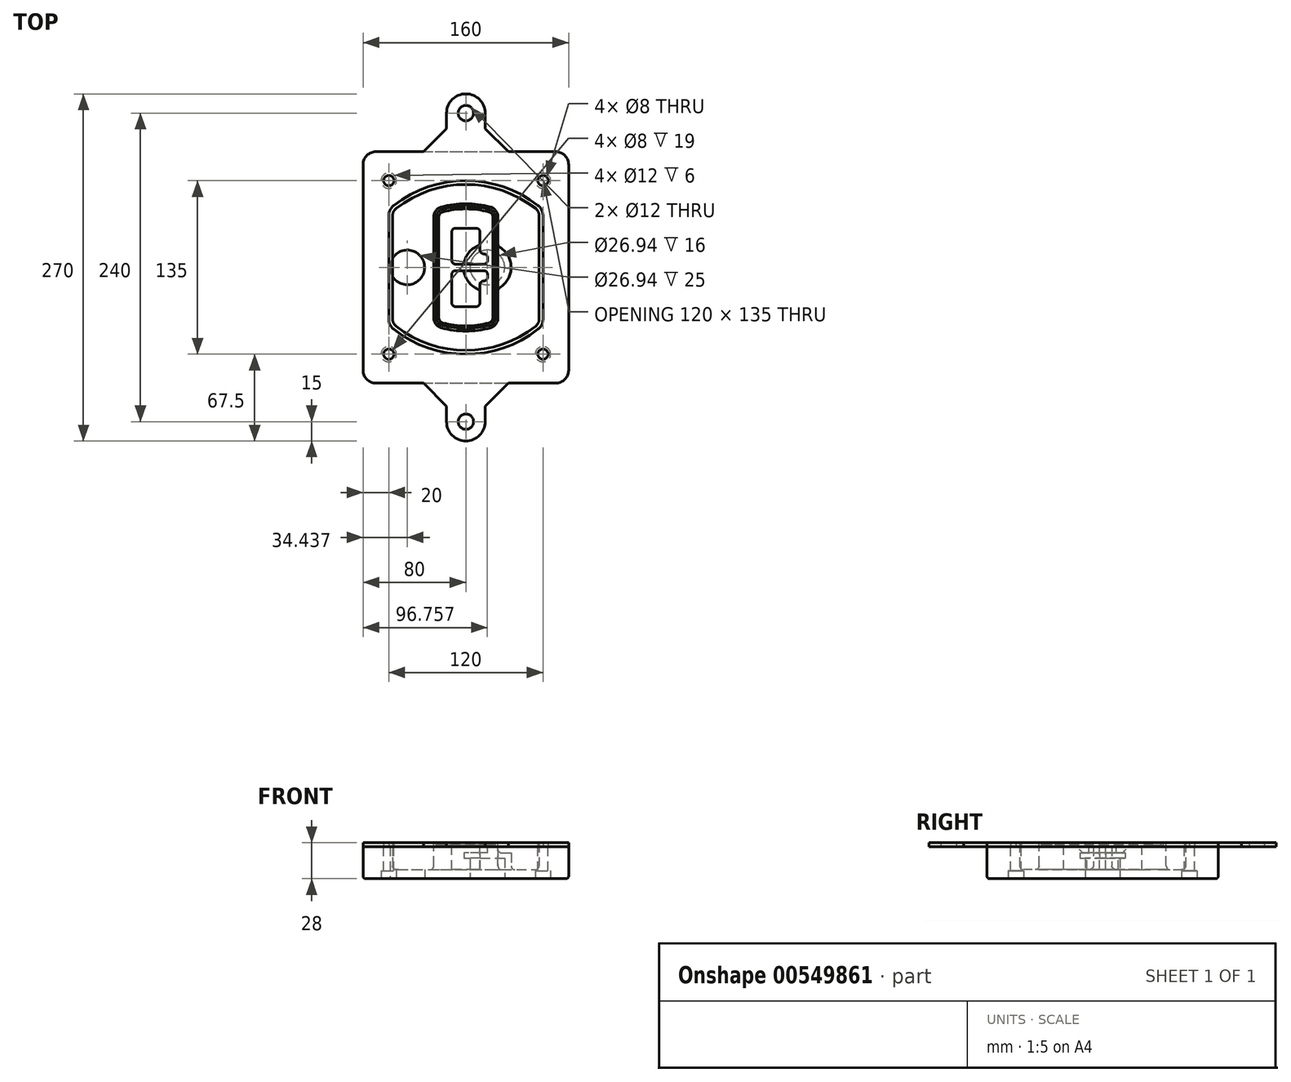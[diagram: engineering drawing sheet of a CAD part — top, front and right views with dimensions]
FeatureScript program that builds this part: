
annotation { "Feature Type Name" : "Feature", "Feature Type Description" : "" }
export const myFeature = defineFeature(function(context is Context, id is Id, definition is map)
    precondition{}
    {
        {
            var Q0;
            Q0=qCreatedBy(makeId("Top.planeOp"),FACE);
            var sketch = newSketch(context, id + "F0", { "sketchPlane" : qUnion([Q0])});
            skPoint(sketch, "E0.rect.middle", {"position": v(0, 0) * mm});
            skLineSegment(sketch, "E1.bottom", {"start": v(-70, -90) * mm, "end": v(70, -90) * mm});
            skLineSegment(sketch, "E1.top", {"start": v(-70, 90) * mm, "end": v(70, 90) * mm});
            skLineSegment(sketch, "E1.left", {"start": v(-80, -80) * mm, "end": v(-80, 80) * mm});
            skLineSegment(sketch, "E1.right", {"start": v(80, -80) * mm, "end": v(80, 80) * mm});
            skLineSegment(sketch, "E2", {"start": v(-80, 90) * mm, "end": v(80, -90) * mm, "construction": true});
            skLineSegment(sketch, "E3", {"start": v(80, 90) * mm, "end": v(-80, -90) * mm, "construction": true});
            skCircle(sketch, "E4", {"center": v(-60, 67.5) * mm, "radius": 4 * mm});
            skCircle(sketch, "E5", {"center": v(60, 67.5) * mm, "radius": 4 * mm});
            skCircle(sketch, "E6", {"center": v(60, -67.5) * mm, "radius": 4 * mm});
            skCircle(sketch, "E7", {"center": v(-60, -67.5) * mm, "radius": 4 * mm});
            skLineSegment(sketch, "E8", {"start": v(-60, 67.5) * mm, "end": v(60, 67.5) * mm, "construction": true});
            skLineSegment(sketch, "E9", {"start": v(60, 67.5) * mm, "end": v(60, -67.5) * mm, "construction": true});
            skLineSegment(sketch, "E10", {"start": v(60, -67.5) * mm, "end": v(-60, -67.5) * mm, "construction": true});
            skLineSegment(sketch, "E11", {"start": v(-60, -67.5) * mm, "end": v(-60, 67.5) * mm, "construction": true});
            skLineSegment(sketch, "E12", {"start": v(-60, 40.3) * mm, "end": v(-60, -40.3) * mm});
            skLineSegment(sketch, "E13", {"start": v(60, 40.3) * mm, "end": v(60, -40.3) * mm});
            skArc(sketch, "E14", {"start": v(56.15, 48.18) * mm, "mid": v(0, 67.5) * mm, "end": v(-56.15, 48.18) * mm});
            skArc(sketch, "E15", {"start": v(-56.15, -48.18) * mm, "mid": v(0, -67.5) * mm, "end": v(56.15, -48.18) * mm});
            skLineSegment(sketch, "E16", {"start": v(-60, 0) * mm, "end": v(60, 0) * mm, "construction": true});
            skPoint(sketch, "E17.visualSharp", {"position": v(-60, -45) * mm});
            skArc(sketch, "E17.filletArc", {"start": v(-60, -40.3) * mm, "mid": v(-58.99, -44.68) * mm, "end": v(-56.15, -48.18) * mm});
            skPoint(sketch, "E18.visualSharp", {"position": v(-60, 45) * mm});
            skArc(sketch, "E18.filletArc", {"start": v(-56.15, 48.18) * mm, "mid": v(-58.99, 44.68) * mm, "end": v(-60, 40.3) * mm});
            skPoint(sketch, "E19.visualSharp", {"position": v(60, 45) * mm});
            skArc(sketch, "E19.filletArc", {"start": v(60, 40.3) * mm, "mid": v(58.99, 44.68) * mm, "end": v(56.15, 48.18) * mm});
            skPoint(sketch, "E20.visualSharp", {"position": v(60, -45) * mm});
            skArc(sketch, "E20.filletArc", {"start": v(56.15, -48.18) * mm, "mid": v(58.99, -44.68) * mm, "end": v(60, -40.3) * mm});
            skPoint(sketch, "E21.visualSharp", {"position": v(-80, 90) * mm});
            skArc(sketch, "E21.filletArc", {"start": v(-70, 90) * mm, "mid": v(-77.07, 87.07) * mm, "end": v(-80, 80) * mm});
            skPoint(sketch, "E22.visualSharp", {"position": v(80, 90) * mm});
            skArc(sketch, "E22.filletArc", {"start": v(80, 80) * mm, "mid": v(77.07, 87.07) * mm, "end": v(70, 90) * mm});
            skPoint(sketch, "E23.visualSharp", {"position": v(80, -90) * mm});
            skArc(sketch, "E23.filletArc", {"start": v(70, -90) * mm, "mid": v(77.07, -87.07) * mm, "end": v(80, -80) * mm});
            skPoint(sketch, "E24.visualSharp", {"position": v(-80, -90) * mm});
            skArc(sketch, "E24.filletArc", {"start": v(-80, -80) * mm, "mid": v(-77.07, -87.07) * mm, "end": v(-70, -90) * mm});
            skArc(sketch, "E25.0", {"start": v(57, 40.3) * mm, "mid": v(56.3, 43.36) * mm, "end": v(54.3, 45.81) * mm});
            skLineSegment(sketch, "E25.1", {"start": v(57, 40.3) * mm, "end": v(57, -40.3) * mm});
            skArc(sketch, "E25.2", {"start": v(54.3, -45.81) * mm, "mid": v(56.3, -43.36) * mm, "end": v(57, -40.3) * mm});
            skArc(sketch, "E25.3", {"start": v(-54.3, -45.81) * mm, "mid": v(0, -64.5) * mm, "end": v(54.3, -45.81) * mm});
            skArc(sketch, "E25.4", {"start": v(-57, -40.3) * mm, "mid": v(-56.3, -43.36) * mm, "end": v(-54.3, -45.81) * mm});
            skArc(sketch, "E25.5", {"start": v(54.3, 45.81) * mm, "mid": v(0, 64.5) * mm, "end": v(-54.3, 45.81) * mm});
            skLineSegment(sketch, "E25.6", {"start": v(-57, 40.3) * mm, "end": v(-57, -40.3) * mm});
            skArc(sketch, "E25.7", {"start": v(-54.3, 45.81) * mm, "mid": v(-56.3, 43.36) * mm, "end": v(-57, 40.3) * mm});
            skArc(sketch, "E26.0", {"start": v(-58.62, 51.33) * mm, "mid": v(-62.58, 46.43) * mm, "end": v(-64, 40.3) * mm});
            skArc(sketch, "E26.1", {"start": v(58.62, 51.33) * mm, "mid": v(0, 71.5) * mm, "end": v(-58.62, 51.33) * mm});
            skArc(sketch, "E26.2", {"start": v(64, 40.3) * mm, "mid": v(62.58, 46.43) * mm, "end": v(58.62, 51.33) * mm});
            skLineSegment(sketch, "E26.3", {"start": v(64, 40.3) * mm, "end": v(64, -40.3) * mm});
            skArc(sketch, "E26.4", {"start": v(58.62, -51.33) * mm, "mid": v(62.58, -46.43) * mm, "end": v(64, -40.3) * mm});
            skLineSegment(sketch, "E26.5", {"start": v(-64, 40.3) * mm, "end": v(-64, -40.3) * mm});
            skArc(sketch, "E26.6", {"start": v(-58.62, -51.33) * mm, "mid": v(0, -71.5) * mm, "end": v(58.62, -51.33) * mm});
            skArc(sketch, "E26.7", {"start": v(-64, -40.3) * mm, "mid": v(-62.58, -46.43) * mm, "end": v(-58.62, -51.33) * mm});
            skSolve(sketch);
        }
        {
            var Q0;
            Q0=makeQuery(id+"F0.imprint","IMPRINT",FACE,{"disambiguationData":[TD([[makeQuery(id+"F0.imprint","IMPRINT",EDGE,{"derivedFrom":sQuery(id+"F0.wireOp",EDGE,"E1.bottom")}),1.0]])]});
            var Q1;
            Q1=makeQuery(id+"F0.imprint","IMPRINT",FACE,{"disambiguationData":[TD([[makeQuery(id+"F0.imprint","IMPRINT",EDGE,{"derivedFrom":sQuery(id+"F0.wireOp",EDGE,"E12")}),1.0]])]});
            var Q2;
            Q2=makeQuery(id+"F0.imprint","IMPRINT",FACE,{"disambiguationData":[TD([[makeQuery(id+"F0.imprint","IMPRINT",EDGE,{"derivedFrom":sQuery(id+"F0.wireOp",EDGE,"E25.0")}),1.0]])]});
            var Q3;
            Q3=makeQuery(id+"F0.imprint","IMPRINT",FACE,{"disambiguationData":[TD([[makeQuery(id+"F0.imprint","IMPRINT",EDGE,{"derivedFrom":sQuery(id+"F0.wireOp",EDGE,"E12")}),-1.0]])]});
            extrude(context, id + "F1", {"entities" : qUnion([Q0, Q1, Q2, Q3]), "oppositeDirection" : true, "depth" : 25 * mm});
        }
        {
            var Q0;
            Q0=makeQuery(id+"F0.imprint","IMPRINT",FACE,{"disambiguationData":[TD([[makeQuery(id+"F0.imprint","IMPRINT",EDGE,{"derivedFrom":sQuery(id+"F0.wireOp",EDGE,"E12")}),1.0]])]});
            extrude(context, id + "F2", {"entities" : qUnion([Q0]), "operationType" : NewBodyOperationType.ADD, "depth" : 3 * mm});
        }
        {
            var Q0;
            Q0=makeQuery(id+"F0.imprint","IMPRINT",FACE,{"disambiguationData":[TD([[makeQuery(id+"F0.imprint","IMPRINT",EDGE,{"derivedFrom":sQuery(id+"F0.wireOp",EDGE,"E25.0")}),1.0]])]});
            extrude(context, id + "F3", {"entities" : qUnion([Q0]), "operationType" : NewBodyOperationType.REMOVE, "oppositeDirection" : true, "depth" : 18 * mm});
        }
        {
            var Q0;
            Q0=makeQuery(id+"F2.opExtrude","CAP_FACE",FACE,{"disambiguationData":[OSD([sQuery(id+"F0.wireOp",EDGE,"E12"),sQuery(id+"F0.wireOp",EDGE,"E13"),sQuery(id+"F0.wireOp",EDGE,"E14"),sQuery(id+"F0.wireOp",EDGE,"E15"),sQuery(id+"F0.wireOp",EDGE,"E17.filletArc"),sQuery(id+"F0.wireOp",EDGE,"E18.filletArc"),sQuery(id+"F0.wireOp",EDGE,"E19.filletArc"),sQuery(id+"F0.wireOp",EDGE,"E20.filletArc"),sQuery(id+"F0.wireOp",EDGE,"E25.0"),sQuery(id+"F0.wireOp",EDGE,"E25.1"),sQuery(id+"F0.wireOp",EDGE,"E25.2"),sQuery(id+"F0.wireOp",EDGE,"E25.3"),sQuery(id+"F0.wireOp",EDGE,"E25.4"),sQuery(id+"F0.wireOp",EDGE,"E25.5"),sQuery(id+"F0.wireOp",EDGE,"E25.6"),sQuery(id+"F0.wireOp",EDGE,"E25.7")])],"isStart":false});
            var sketch = newSketch(context, id + "F4", { "sketchPlane" : qUnion([Q0])});
            skArc(sketch, "E27.0", {"start": v(-19.08, -46.97) * mm, "mid": v(0, -49.5) * mm, "end": v(19.08, -46.97) * mm});
            skArc(sketch, "E28.0", {"start": v(19.08, 46.97) * mm, "mid": v(0, 49.5) * mm, "end": v(-19.08, 46.97) * mm});
            skLineSegment(sketch, "E29", {"start": v(-25, 39.25) * mm, "end": v(-25, -39.25) * mm});
            skLineSegment(sketch, "E30", {"start": v(25, 39.25) * mm, "end": v(25, -39.25) * mm});
            skLineSegment(sketch, "E31", {"start": v(-25, 45.1) * mm, "end": v(25, 45.1) * mm, "construction": true});
            skLineSegment(sketch, "E32", {"start": v(-25, -45.1) * mm, "end": v(25, -45.1) * mm, "construction": true});
            skPoint(sketch, "E33.visualSharp", {"position": v(-25, 45.1) * mm});
            skArc(sketch, "E33.filletArc", {"start": v(-19.08, 46.97) * mm, "mid": v(-23.35, 44.11) * mm, "end": v(-25, 39.25) * mm});
            skPoint(sketch, "E34.visualSharp", {"position": v(25, 45.1) * mm});
            skArc(sketch, "E34.filletArc", {"start": v(25, 39.25) * mm, "mid": v(23.35, 44.11) * mm, "end": v(19.08, 46.97) * mm});
            skPoint(sketch, "E35.visualSharp", {"position": v(25, -45.1) * mm});
            skArc(sketch, "E35.filletArc", {"start": v(19.08, -46.97) * mm, "mid": v(23.35, -44.11) * mm, "end": v(25, -39.25) * mm});
            skPoint(sketch, "E36.visualSharp", {"position": v(-25, -45.1) * mm});
            skArc(sketch, "E36.filletArc", {"start": v(-25, -39.25) * mm, "mid": v(-23.35, -44.11) * mm, "end": v(-19.08, -46.97) * mm});
            skArc(sketch, "E37.0", {"start": v(54.3, 45.81) * mm, "mid": v(0, 64.5) * mm, "end": v(-54.3, 45.81) * mm});
            skArc(sketch, "E37.1", {"start": v(-54.3, 45.81) * mm, "mid": v(-56.3, 43.36) * mm, "end": v(-57, 40.3) * mm});
            skLineSegment(sketch, "E37.2", {"start": v(-57, 40.3) * mm, "end": v(-57, -40.3) * mm});
            skArc(sketch, "E37.3", {"start": v(-57, -40.3) * mm, "mid": v(-56.3, -43.36) * mm, "end": v(-54.3, -45.81) * mm});
            skArc(sketch, "E37.4", {"start": v(-54.3, -45.81) * mm, "mid": v(0, -64.5) * mm, "end": v(54.3, -45.81) * mm});
            skArc(sketch, "E37.5", {"start": v(54.3, -45.81) * mm, "mid": v(56.3, -43.36) * mm, "end": v(57, -40.3) * mm});
            skLineSegment(sketch, "E37.6", {"start": v(57, 40.3) * mm, "end": v(57, -40.3) * mm});
            skArc(sketch, "E37.7", {"start": v(57, 40.3) * mm, "mid": v(56.3, 43.36) * mm, "end": v(54.3, 45.81) * mm});
            skLineSegment(sketch, "E38.0", {"start": v(23, 39.25) * mm, "end": v(23, -39.25) * mm});
            skArc(sketch, "E38.1", {"start": v(18.56, -45.04) * mm, "mid": v(21.76, -42.9) * mm, "end": v(23, -39.25) * mm});
            skArc(sketch, "E38.2", {"start": v(-18.56, -45.04) * mm, "mid": v(0, -47.5) * mm, "end": v(18.56, -45.04) * mm});
            skArc(sketch, "E38.3", {"start": v(-23, -39.25) * mm, "mid": v(-21.76, -42.9) * mm, "end": v(-18.56, -45.04) * mm});
            skLineSegment(sketch, "E38.4", {"start": v(-23, 39.25) * mm, "end": v(-23, -39.25) * mm});
            skArc(sketch, "E38.5", {"start": v(23, 39.25) * mm, "mid": v(21.76, 42.9) * mm, "end": v(18.56, 45.04) * mm});
            skArc(sketch, "E38.6", {"start": v(-18.56, 45.04) * mm, "mid": v(-21.76, 42.9) * mm, "end": v(-23, 39.25) * mm});
            skArc(sketch, "E38.7", {"start": v(18.56, 45.04) * mm, "mid": v(0, 47.5) * mm, "end": v(-18.56, 45.04) * mm});
            skArc(sketch, "E39.0", {"start": v(21, 39.25) * mm, "mid": v(20.18, 41.68) * mm, "end": v(18.04, 43.1) * mm});
            skLineSegment(sketch, "E39.1", {"start": v(21, 39.25) * mm, "end": v(21, -39.25) * mm});
            skArc(sketch, "E39.2", {"start": v(18.04, -43.1) * mm, "mid": v(20.18, -41.68) * mm, "end": v(21, -39.25) * mm});
            skArc(sketch, "E39.3", {"start": v(-18.04, -43.1) * mm, "mid": v(0, -45.5) * mm, "end": v(18.04, -43.1) * mm});
            skArc(sketch, "E39.4", {"start": v(-21, -39.25) * mm, "mid": v(-20.18, -41.68) * mm, "end": v(-18.04, -43.1) * mm});
            skArc(sketch, "E39.5", {"start": v(18.04, 43.1) * mm, "mid": v(0, 45.5) * mm, "end": v(-18.04, 43.1) * mm});
            skLineSegment(sketch, "E39.6", {"start": v(-21, 39.25) * mm, "end": v(-21, -39.25) * mm});
            skArc(sketch, "E39.7", {"start": v(-18.04, 43.1) * mm, "mid": v(-20.18, 41.68) * mm, "end": v(-21, 39.25) * mm});
            skLineSegment(sketch, "E40", {"start": v(-25, 0) * mm, "end": v(25, 0) * mm, "construction": true});
            skLineSegment(sketch, "E41", {"start": v(-11, 5.5) * mm, "end": v(-11, 27.5) * mm});
            skLineSegment(sketch, "E42", {"start": v(-8, 30.5) * mm, "end": v(8, 30.5) * mm});
            skLineSegment(sketch, "E43", {"start": v(11, 27.5) * mm, "end": v(11, 13.5) * mm});
            skLineSegment(sketch, "E44", {"start": v(14, 10.5) * mm, "end": v(14, 10.5) * mm});
            skLineSegment(sketch, "E45", {"start": v(17, 7.5) * mm, "end": v(17, 5.5) * mm});
            skLineSegment(sketch, "E46", {"start": v(14, 2.5) * mm, "end": v(-8, 2.5) * mm});
            skPoint(sketch, "E47.visualSharp", {"position": v(-11, 30.5) * mm});
            skArc(sketch, "E47.filletArc", {"start": v(-8, 30.5) * mm, "mid": v(-10.12, 29.62) * mm, "end": v(-11, 27.5) * mm});
            skPoint(sketch, "E48.visualSharp", {"position": v(11, 30.5) * mm});
            skArc(sketch, "E48.filletArc", {"start": v(11, 27.5) * mm, "mid": v(10.12, 29.62) * mm, "end": v(8, 30.5) * mm});
            skPoint(sketch, "E49.visualSharp", {"position": v(11, 10.5) * mm});
            skArc(sketch, "E49.filletArc", {"start": v(11, 13.5) * mm, "mid": v(11.88, 11.38) * mm, "end": v(14, 10.5) * mm});
            skPoint(sketch, "E50.visualSharp", {"position": v(17, 10.5) * mm});
            skArc(sketch, "E50.filletArc", {"start": v(17, 7.5) * mm, "mid": v(16.12, 9.62) * mm, "end": v(14, 10.5) * mm});
            skPoint(sketch, "E51.visualSharp", {"position": v(17, 2.5) * mm});
            skArc(sketch, "E51.filletArc", {"start": v(14, 2.5) * mm, "mid": v(16.12, 3.38) * mm, "end": v(17, 5.5) * mm});
            skPoint(sketch, "E52.visualSharp", {"position": v(-11, 2.5) * mm});
            skArc(sketch, "E52.filletArc", {"start": v(-11, 5.5) * mm, "mid": v(-10.12, 3.38) * mm, "end": v(-8, 2.5) * mm});
            skLineSegment(sketch, "E53.0.MirrorCS", {"start": v(14, -2.5) * mm, "end": v(-8, -2.5) * mm});
            skArc(sketch, "E54.0.MirrorCS", {"start": v(-11, -5.5) * mm, "mid": v(-10.12, -3.38) * mm, "end": v(-8, -2.5) * mm});
            skLineSegment(sketch, "E55.0.MirrorCS", {"start": v(-11, -5.5) * mm, "end": v(-11, -27.5) * mm});
            skArc(sketch, "E56.0.MirrorCS", {"start": v(-8, -30.5) * mm, "mid": v(-10.12, -29.62) * mm, "end": v(-11, -27.5) * mm});
            skLineSegment(sketch, "E57.0.MirrorCS", {"start": v(-8, -30.5) * mm, "end": v(8, -30.5) * mm});
            skArc(sketch, "E58.0.MirrorCS", {"start": v(11, -27.5) * mm, "mid": v(10.12, -29.62) * mm, "end": v(8, -30.5) * mm});
            skLineSegment(sketch, "E59.0.MirrorCS", {"start": v(11, -27.5) * mm, "end": v(11, -13.5) * mm});
            skArc(sketch, "E60.0.MirrorCS", {"start": v(11, -13.5) * mm, "mid": v(11.88, -11.38) * mm, "end": v(14, -10.5) * mm});
            skArc(sketch, "E61.0.MirrorCS", {"start": v(17, -7.5) * mm, "mid": v(16.12, -9.62) * mm, "end": v(14, -10.5) * mm});
            skLineSegment(sketch, "E62.0.MirrorCS", {"start": v(17, -7.5) * mm, "end": v(17, -5.5) * mm});
            skArc(sketch, "E63.0.MirrorCS", {"start": v(14, -2.5) * mm, "mid": v(16.12, -3.38) * mm, "end": v(17, -5.5) * mm});
            skSolve(sketch);
        }
        {
            var Q0;
            Q0=makeQuery(id+"F4.imprint","IMPRINT",FACE,{"disambiguationData":[TD([[makeQuery(id+"F4.imprint","IMPRINT",EDGE,{"derivedFrom":sQuery(id+"F4.wireOp",EDGE,"E27.0")}),1.0]])]});
            var Q1;
            Q1=makeQuery(id+"F4.imprint","IMPRINT",FACE,{"disambiguationData":[TD([[makeQuery(id+"F4.imprint","IMPRINT",EDGE,{"derivedFrom":sQuery(id+"F4.wireOp",EDGE,"E38.0")}),-1.0]])]});
            var Q2;
            Q2=makeQuery(id+"F4.imprint","IMPRINT",FACE,{"disambiguationData":[TD([[makeQuery(id+"F4.imprint","IMPRINT",EDGE,{"derivedFrom":sQuery(id+"F4.wireOp",EDGE,"E39.0")}),1.0]])]});
            extrude(context, id + "F5", {"entities" : qUnion([Q0, Q1, Q2]), "operationType" : NewBodyOperationType.ADD, "endBound" : BoundingType.UP_TO_NEXT, "oppositeDirection" : true, "depth" : 25 * mm});
        }
        {
            var Q0;
            Q0=makeQuery(id+"F4.imprint","IMPRINT",FACE,{"disambiguationData":[TD([[makeQuery(id+"F4.imprint","IMPRINT",EDGE,{"derivedFrom":sQuery(id+"F4.wireOp",EDGE,"E38.0")}),-1.0]])]});
            extrude(context, id + "F6", {"entities" : qUnion([Q0]), "operationType" : NewBodyOperationType.REMOVE, "oppositeDirection" : true, "depth" : 2 * mm});
        }
        {
            var Q0;
            Q0=makeQuery(id+"F1.opExtrude","CAP_FACE",FACE,{"disambiguationData":[OSD([sQuery(id+"F0.wireOp",EDGE,"E1.bottom"),sQuery(id+"F0.wireOp",EDGE,"E1.top"),sQuery(id+"F0.wireOp",EDGE,"E1.left"),sQuery(id+"F0.wireOp",EDGE,"E1.right"),sQuery(id+"F0.wireOp",EDGE,"E4"),sQuery(id+"F0.wireOp",EDGE,"E5"),sQuery(id+"F0.wireOp",EDGE,"E6"),sQuery(id+"F0.wireOp",EDGE,"E7"),sQuery(id+"F0.wireOp",EDGE,"E21.filletArc"),sQuery(id+"F0.wireOp",EDGE,"E22.filletArc"),sQuery(id+"F0.wireOp",EDGE,"E23.filletArc"),sQuery(id+"F0.wireOp",EDGE,"E24.filletArc")])],"isStart":false});
            var sketch = newSketch(context, id + "F7", { "sketchPlane" : qUnion([Q0])});
            skCircle(sketch, "E64", {"center": v(16.76, 0) * mm, "radius": 13.47 * mm});
            skCircle(sketch, "E65", {"center": v(-45.56, 0) * mm, "radius": 13.47 * mm});
            skLineSegment(sketch, "E66", {"start": v(80, 0) * mm, "end": v(-80, 0) * mm});
            skCircle(sketch, "E67", {"center": v(16.76, 0) * mm, "radius": 18.47 * mm});
            skCircle(sketch, "E68", {"center": v(60, -67.5) * mm, "radius": 6 * mm});
            skCircle(sketch, "E69", {"center": v(-60, -67.5) * mm, "radius": 6 * mm});
            skCircle(sketch, "E70", {"center": v(-60, 67.5) * mm, "radius": 6 * mm});
            skCircle(sketch, "E71", {"center": v(60, 67.5) * mm, "radius": 6 * mm});
            skSolve(sketch);
        }
        {
            var Q0;
            {var subQ1=sQuery(id+"F7.wireOp",EDGE,"E66");var subQ4=sQuery(id+"F7.wireOp",EDGE,"E64");var subQ6=makeQuery(id+"F7.imprint","INTERSECT",VERTEX,{"disambiguationData":[OD(0.0)],"derivedFrom":[subQ4,subQ1]});Q0=makeQuery(id+"F7.imprint","IMPRINT",FACE,{"disambiguationData":[TD([[makeQuery(id+"F7.imprint","IMPRINT",EDGE,{"disambiguationData":[TD([[subQ6,-1.0]])],"derivedFrom":subQ4}),-1.0]])]});}
            var Q1;
            {var subQ0=sQuery(id+"F7.wireOp",EDGE,"E66");var subQ1=sQuery(id+"F7.wireOp",EDGE,"E64");var subQ3=makeQuery(id+"F7.imprint","INTERSECT",VERTEX,{"disambiguationData":[OD(0.0)],"derivedFrom":[subQ1,subQ0]});Q1=makeQuery(id+"F7.imprint","IMPRINT",FACE,{"disambiguationData":[TD([[makeQuery(id+"F7.imprint","IMPRINT",EDGE,{"disambiguationData":[TD([[subQ3,-1.0]])],"derivedFrom":subQ1}),1.0]])]});}
            var Q2;
            {var subQ0=sQuery(id+"F7.wireOp",EDGE,"E66");var subQ1=sQuery(id+"F7.wireOp",EDGE,"E64");var subQ3=makeQuery(id+"F7.imprint","INTERSECT",VERTEX,{"disambiguationData":[OD(0.0)],"derivedFrom":[subQ1,subQ0]});Q2=makeQuery(id+"F7.imprint","IMPRINT",FACE,{"disambiguationData":[TD([[makeQuery(id+"F7.imprint","IMPRINT",EDGE,{"disambiguationData":[TD([[subQ3,1.0]])],"derivedFrom":subQ1}),1.0]])]});}
            var Q3;
            {var subQ1=sQuery(id+"F7.wireOp",EDGE,"E66");var subQ4=sQuery(id+"F7.wireOp",EDGE,"E64");var subQ6=makeQuery(id+"F7.imprint","INTERSECT",VERTEX,{"disambiguationData":[OD(0.0)],"derivedFrom":[subQ4,subQ1]});Q3=makeQuery(id+"F7.imprint","IMPRINT",FACE,{"disambiguationData":[TD([[makeQuery(id+"F7.imprint","IMPRINT",EDGE,{"disambiguationData":[TD([[subQ6,1.0]])],"derivedFrom":subQ4}),-1.0]])]});}
            extrude(context, id + "F8", {"entities" : qUnion([Q0, Q1, Q2, Q3]), "operationType" : NewBodyOperationType.ADD, "oppositeDirection" : true, "depth" : 20 * mm});
        }
        {
            var Q0;
            {var subQ0=sQuery(id+"F7.wireOp",EDGE,"E66");var subQ1=sQuery(id+"F7.wireOp",EDGE,"E64");var subQ3=makeQuery(id+"F7.imprint","INTERSECT",VERTEX,{"disambiguationData":[OD(0.0)],"derivedFrom":[subQ1,subQ0]});Q0=makeQuery(id+"F7.imprint","IMPRINT",FACE,{"disambiguationData":[TD([[makeQuery(id+"F7.imprint","IMPRINT",EDGE,{"disambiguationData":[TD([[subQ3,-1.0]])],"derivedFrom":subQ1}),1.0]])]});}
            var Q1;
            {var subQ0=sQuery(id+"F7.wireOp",EDGE,"E66");var subQ1=sQuery(id+"F7.wireOp",EDGE,"E64");var subQ3=makeQuery(id+"F7.imprint","INTERSECT",VERTEX,{"disambiguationData":[OD(0.0)],"derivedFrom":[subQ1,subQ0]});Q1=makeQuery(id+"F7.imprint","IMPRINT",FACE,{"disambiguationData":[TD([[makeQuery(id+"F7.imprint","IMPRINT",EDGE,{"disambiguationData":[TD([[subQ3,1.0]])],"derivedFrom":subQ1}),1.0]])]});}
            extrude(context, id + "F9", {"entities" : qUnion([Q0, Q1]), "operationType" : NewBodyOperationType.REMOVE, "oppositeDirection" : true, "depth" : 16 * mm});
        }
        {
            var Q0;
            {var subQ0=sQuery(id+"F7.wireOp",EDGE,"E66");var subQ1=sQuery(id+"F7.wireOp",EDGE,"E65");var subQ3=makeQuery(id+"F7.imprint","INTERSECT",VERTEX,{"disambiguationData":[OD(0.0)],"derivedFrom":[subQ1,subQ0]});Q0=makeQuery(id+"F7.imprint","IMPRINT",FACE,{"disambiguationData":[TD([[makeQuery(id+"F7.imprint","IMPRINT",EDGE,{"disambiguationData":[TD([[subQ3,-1.0]])],"derivedFrom":subQ1}),1.0]])]});}
            var Q1;
            {var subQ0=sQuery(id+"F7.wireOp",EDGE,"E66");var subQ1=sQuery(id+"F7.wireOp",EDGE,"E65");var subQ3=makeQuery(id+"F7.imprint","INTERSECT",VERTEX,{"disambiguationData":[OD(0.0)],"derivedFrom":[subQ1,subQ0]});Q1=makeQuery(id+"F7.imprint","IMPRINT",FACE,{"disambiguationData":[TD([[makeQuery(id+"F7.imprint","IMPRINT",EDGE,{"disambiguationData":[TD([[subQ3,1.0]])],"derivedFrom":subQ1}),1.0]])]});}
            extrude(context, id + "F10", {"entities" : qUnion([Q0, Q1]), "operationType" : NewBodyOperationType.REMOVE, "oppositeDirection" : true, "depth" : 25 * mm});
        }
        {
            var Q0;
            Q0=makeQuery(id+"F7.imprint","IMPRINT",FACE,{"disambiguationData":[TD([[makeQuery(id+"F7.imprint","IMPRINT",EDGE,{"derivedFrom":sQuery(id+"F7.wireOp",EDGE,"E68")}),1.0]])]});
            var Q1;
            Q1=makeQuery(id+"F7.imprint","IMPRINT",FACE,{"disambiguationData":[TD([[makeQuery(id+"F7.imprint","IMPRINT",EDGE,{"derivedFrom":makeQuery(id+"F1.opExtrude","CAP_EDGE",EDGE,{"disambiguationData":[OSD([sQuery(id+"F0.wireOp",EDGE,"E5")])],"isStart":false})}),-1.0]])]});
            var Q2;
            Q2=makeQuery(id+"F7.imprint","IMPRINT",FACE,{"disambiguationData":[TD([[makeQuery(id+"F7.imprint","IMPRINT",EDGE,{"derivedFrom":sQuery(id+"F7.wireOp",EDGE,"E69")}),1.0]])]});
            var Q3;
            Q3=makeQuery(id+"F7.imprint","IMPRINT",FACE,{"disambiguationData":[TD([[makeQuery(id+"F7.imprint","IMPRINT",EDGE,{"derivedFrom":makeQuery(id+"F1.opExtrude","CAP_EDGE",EDGE,{"disambiguationData":[OSD([sQuery(id+"F0.wireOp",EDGE,"E4")])],"isStart":false})}),-1.0]])]});
            var Q4;
            Q4=makeQuery(id+"F7.imprint","IMPRINT",FACE,{"disambiguationData":[TD([[makeQuery(id+"F7.imprint","IMPRINT",EDGE,{"derivedFrom":sQuery(id+"F7.wireOp",EDGE,"E70")}),1.0]])]});
            var Q5;
            Q5=makeQuery(id+"F7.imprint","IMPRINT",FACE,{"disambiguationData":[TD([[makeQuery(id+"F7.imprint","IMPRINT",EDGE,{"derivedFrom":makeQuery(id+"F1.opExtrude","CAP_EDGE",EDGE,{"disambiguationData":[OSD([sQuery(id+"F0.wireOp",EDGE,"E7")])],"isStart":false})}),-1.0]])]});
            var Q6;
            Q6=makeQuery(id+"F7.imprint","IMPRINT",FACE,{"disambiguationData":[TD([[makeQuery(id+"F7.imprint","IMPRINT",EDGE,{"derivedFrom":sQuery(id+"F7.wireOp",EDGE,"E71")}),1.0]])]});
            var Q7;
            Q7=makeQuery(id+"F7.imprint","IMPRINT",FACE,{"disambiguationData":[TD([[makeQuery(id+"F7.imprint","IMPRINT",EDGE,{"derivedFrom":makeQuery(id+"F1.opExtrude","CAP_EDGE",EDGE,{"disambiguationData":[OSD([sQuery(id+"F0.wireOp",EDGE,"E6")])],"isStart":false})}),-1.0]])]});
            extrude(context, id + "F11", {"entities" : qUnion([Q0, Q1, Q2, Q3, Q4, Q5, Q6, Q7]), "operationType" : NewBodyOperationType.REMOVE, "oppositeDirection" : true, "depth" : 6 * mm});
        }
        {
            var Q0;
            Q0=makeQuery(id+"F9.boolean.opBoolean","COPY",FACE,{"derivedFrom":makeQuery(id+"F9.opExtrude","CAP_FACE",FACE,{"disambiguationData":[OSD([sQuery(id+"F7.wireOp",EDGE,"E64")])],"isStart":false})});
            var sketch = newSketch(context, id + "F12", { "sketchPlane" : qUnion([Q0])});
            skArc(sketch, "E72.0", {"start": v(11, 17.55) * mm, "mid": v(2.57, 11.82) * mm, "end": v(-1.54, 2.5) * mm});
            skArc(sketch, "E72.1", {"start": v(-1.54, -2.5) * mm, "mid": v(2.57, -11.82) * mm, "end": v(11, -17.55) * mm});
            skLineSegment(sketch, "E73", {"start": v(-1.54, -2.5) * mm, "end": v(14, -2.5) * mm});
            skLineSegment(sketch, "E74.0", {"start": v(14, 2.5) * mm, "end": v(-1.54, 2.5) * mm});
            skArc(sketch, "E74.1", {"start": v(14, 2.5) * mm, "mid": v(16.12, 3.38) * mm, "end": v(17, 5.5) * mm});
            skLineSegment(sketch, "E74.2", {"start": v(17, 7.5) * mm, "end": v(17, 5.5) * mm});
            skArc(sketch, "E74.3", {"start": v(17, 7.5) * mm, "mid": v(16.12, 9.62) * mm, "end": v(14, 10.5) * mm});
            skArc(sketch, "E74.4", {"start": v(11, 13.5) * mm, "mid": v(11.88, 11.38) * mm, "end": v(14, 10.5) * mm});
            skLineSegment(sketch, "E74.5", {"start": v(11, 17.55) * mm, "end": v(11, 13.5) * mm});
            skLineSegment(sketch, "E74.7", {"start": v(14, -2.5) * mm, "end": v(-1.54, -2.5) * mm});
            skArc(sketch, "E74.8", {"start": v(14, -2.5) * mm, "mid": v(16.12, -3.38) * mm, "end": v(17, -5.5) * mm});
            skLineSegment(sketch, "E74.9", {"start": v(17, -7.5) * mm, "end": v(17, -5.5) * mm});
            skArc(sketch, "E74.10", {"start": v(17, -7.5) * mm, "mid": v(16.12, -9.62) * mm, "end": v(14, -10.5) * mm});
            skArc(sketch, "E74.11", {"start": v(11, -13.5) * mm, "mid": v(11.88, -11.38) * mm, "end": v(14, -10.5) * mm});
            skLineSegment(sketch, "E74.12", {"start": v(11, -17.55) * mm, "end": v(11, -13.5) * mm});
            skPoint(sketch, "E75.orphan", {"position": v(11, -27.5) * mm});
            skPoint(sketch, "E76.orphan", {"position": v(-8, -2.5) * mm});
            skPoint(sketch, "E77.orphan", {"position": v(-8, 2.5) * mm});
            skPoint(sketch, "E78.orphan", {"position": v(11, 27.5) * mm});
            skSolve(sketch);
        }
        {
            var Q0;
            {var subQ7=sQuery(id+"F12.wireOp",EDGE,"E72.0");var subQ14=sQuery(id+"F12.wireOp",EDGE,"E72.1");var subQ16=sQuery(id+"F12.wireOp",EDGE,"E74.1");var subQ18=sQuery(id+"F12.wireOp",EDGE,"E74.8");Q0=qUnion([makeQuery(id+"F12.imprint","IMPRINT",FACE,{"disambiguationData":[TD([[makeQuery(id+"F12.imprint","IMPRINT",EDGE,{"derivedFrom":subQ7}),1.0]])]}),makeQuery(id+"F12.imprint","IMPRINT",FACE,{"disambiguationData":[TD([[makeQuery(id+"F12.imprint","IMPRINT",EDGE,{"derivedFrom":subQ14}),1.0]])]}),makeQuery(id+"F12.imprint","IMPRINT",FACE,{"disambiguationData":[TD([[makeQuery(id+"F12.imprint","IMPRINT",EDGE,{"derivedFrom":subQ16}),1.0]])]}),makeQuery(id+"F12.imprint","IMPRINT",FACE,{"disambiguationData":[TD([[makeQuery(id+"F12.imprint","IMPRINT",EDGE,{"derivedFrom":subQ18}),-1.0]])]})]);}
            var Q1;
            Q1=makeQuery(id+"F5.boolean.opBoolean","SPLIT",FACE,{"disambiguationData":[TD([makeQuery(id+"F5.opExtrude","SWEPT_FACE",FACE,{"disambiguationData":[OSD([sQuery(id+"F4.wireOp",EDGE,"E41")])]})])],"derivedFrom":makeQuery(id+"F3.boolean.opBoolean","COPY",FACE,{"derivedFrom":makeQuery(id+"F3.opExtrude","CAP_FACE",FACE,{"disambiguationData":[OSD([sQuery(id+"F0.wireOp",EDGE,"E25.0"),sQuery(id+"F0.wireOp",EDGE,"E25.1"),sQuery(id+"F0.wireOp",EDGE,"E25.2"),sQuery(id+"F0.wireOp",EDGE,"E25.3"),sQuery(id+"F0.wireOp",EDGE,"E25.4"),sQuery(id+"F0.wireOp",EDGE,"E25.5"),sQuery(id+"F0.wireOp",EDGE,"E25.6"),sQuery(id+"F0.wireOp",EDGE,"E25.7")])],"isStart":false})})});
            extrude(context, id + "F13", {"entities" : qUnion([Q0]), "operationType" : NewBodyOperationType.REMOVE, "endBound" : BoundingType.UP_TO_SURFACE, "endBoundEntityFace" : qUnion([Q1]), "depth" : 25 * mm});
        }
        {
            var Q0;
            Q0=makeQuery(id+"F3.boolean.opBoolean","COPY",EDGE,{"derivedFrom":makeQuery(id+"F3.opExtrude","CAP_EDGE",EDGE,{"disambiguationData":[OSD([sQuery(id+"F0.wireOp",EDGE,"E25.6")])],"isStart":false})});
            var Q1;
            Q1=makeQuery(id+"F8.boolean.opBoolean","INTERSECT",EDGE,{"derivedFrom":[makeQuery(id+"F5.opExtrude","SWEPT_FACE",FACE,{"disambiguationData":[OSD([sQuery(id+"F4.wireOp",EDGE,"E30")])]}),makeQuery(id+"F8.opExtrude","CAP_FACE",FACE,{"disambiguationData":[OSD([sQuery(id+"F7.wireOp",EDGE,"E67")])],"isStart":false})]});
            var Q2;
            Q2=makeQuery(id+"F8.boolean.opBoolean","INTERSECT",EDGE,{"disambiguationData":[OD(1.0)],"derivedFrom":[makeQuery(id+"F5.opExtrude","SWEPT_FACE",FACE,{"disambiguationData":[OSD([sQuery(id+"F4.wireOp",EDGE,"E30")])]}),makeQuery(id+"F8.opExtrude","SWEPT_FACE",FACE,{"disambiguationData":[OSD([sQuery(id+"F7.wireOp",EDGE,"E67")])]})]});
            var Q3;
            {var subQ0=sQuery(id+"F4.wireOp",EDGE,"E30");Q3=makeQuery(id+"F8.boolean.opBoolean","SPLIT",EDGE,{"disambiguationData":[TD([makeQuery(id+"F5.opExtrude","SWEPT_FACE",FACE,{"disambiguationData":[OSD([sQuery(id+"F4.wireOp",EDGE,"E35.filletArc")])]})])],"derivedFrom":makeQuery(id+"F5.opExtrude","CAP_EDGE",EDGE,{"disambiguationData":[OSD([subQ0])],"isStart":false})});}
            var Q4;
            {var subQ0=sQuery(id+"F0.wireOp",EDGE,"E25.7");var subQ1=sQuery(id+"F0.wireOp",EDGE,"E25.1");var subQ2=sQuery(id+"F0.wireOp",EDGE,"E25.6");var subQ3=sQuery(id+"F0.wireOp",EDGE,"E25.5");var subQ4=sQuery(id+"F0.wireOp",EDGE,"E25.4");var subQ5=sQuery(id+"F0.wireOp",EDGE,"E25.0");var subQ6=sQuery(id+"F0.wireOp",EDGE,"E25.2");var subQ7=sQuery(id+"F0.wireOp",EDGE,"E25.3");Q4=makeQuery(id+"F8.boolean.opBoolean","INTERSECT",EDGE,{"derivedFrom":[makeQuery(id+"F5.boolean.opBoolean","SPLIT",FACE,{"disambiguationData":[TD([makeQuery(id+"F2.opExtrude","SWEPT_FACE",FACE,{"disambiguationData":[OSD([subQ5])]})])],"derivedFrom":makeQuery(id+"F3.boolean.opBoolean","COPY",FACE,{"derivedFrom":makeQuery(id+"F3.opExtrude","CAP_FACE",FACE,{"disambiguationData":[OSD([subQ5,subQ1,subQ6,subQ7,subQ4,subQ3,subQ2,subQ0])],"isStart":false})})}),makeQuery(id+"F8.opExtrude","SWEPT_FACE",FACE,{"disambiguationData":[OSD([sQuery(id+"F7.wireOp",EDGE,"E67")])]})]});}
            var Q5;
            Q5=makeQuery(id+"F8.boolean.opBoolean","INTERSECT",EDGE,{"disambiguationData":[OD(0.0)],"derivedFrom":[makeQuery(id+"F5.opExtrude","SWEPT_FACE",FACE,{"disambiguationData":[OSD([sQuery(id+"F4.wireOp",EDGE,"E30")])]}),makeQuery(id+"F8.opExtrude","SWEPT_FACE",FACE,{"disambiguationData":[OSD([sQuery(id+"F7.wireOp",EDGE,"E67")])]})]});
            fillet(context, id + "F14", {"entities" : qUnion([Q0, Q1, Q2, Q3, Q4, Q5]), "radius" : 3 * mm, "tangentPropagation" : true, "allowEdgeOverflow" : false});
        }
        {
            var Q0;
            Q0=makeQuery(id+"F1.opExtrude","CAP_EDGE",EDGE,{"disambiguationData":[OSD([sQuery(id+"F0.wireOp",EDGE,"E1.bottom")])],"isStart":false});
            fillet(context, id + "F15", {"entities" : qUnion([Q0]), "radius" : 2 * mm, "tangentPropagation" : true, "allowEdgeOverflow" : false});
        }
        {
            var Q0;
            {var subQ0=sQuery(id+"F0.wireOp",EDGE,"E21.filletArc");var subQ1=sQuery(id+"F0.wireOp",EDGE,"E7");var subQ2=sQuery(id+"F0.wireOp",EDGE,"E6");var subQ3=sQuery(id+"F0.wireOp",EDGE,"E5");var subQ4=sQuery(id+"F0.wireOp",EDGE,"E4");var subQ5=sQuery(id+"F0.wireOp",EDGE,"E22.filletArc");var subQ6=sQuery(id+"F0.wireOp",EDGE,"E1.bottom");var subQ7=sQuery(id+"F0.wireOp",EDGE,"E1.right");var subQ8=sQuery(id+"F0.wireOp",EDGE,"E1.top");var subQ9=sQuery(id+"F0.wireOp",EDGE,"E1.left");var subQ10=sQuery(id+"F0.wireOp",EDGE,"E23.filletArc");var subQ11=sQuery(id+"F0.wireOp",EDGE,"E24.filletArc");Q0=makeQuery(id+"F2.boolean.opBoolean","SPLIT",FACE,{"disambiguationData":[TD([makeQuery(id+"F1.opExtrude","SWEPT_FACE",FACE,{"disambiguationData":[OSD([subQ6])]})])],"derivedFrom":makeQuery(id+"F1.opExtrude","CAP_FACE",FACE,{"disambiguationData":[OSD([subQ6,subQ8,subQ9,subQ7,subQ4,subQ3,subQ2,subQ1,subQ0,subQ5,subQ10,subQ11])],"isStart":true})});}
            var sketch = newSketch(context, id + "F16", { "sketchPlane" : qUnion([Q0])});
            skLineSegment(sketch, "E79", {"start": v(0, 90) * mm, "end": v(0, 120) * mm, "construction": true});
            skCircle(sketch, "E80", {"center": v(0, 120) * mm, "radius": 6 * mm});
            skArc(sketch, "E81", {"start": v(-15, 120) * mm, "mid": v(0, 135) * mm, "end": v(15, 120) * mm});
            skLineSegment(sketch, "E82", {"start": v(-15, 120) * mm, "end": v(-15, 108) * mm});
            skLineSegment(sketch, "E83", {"start": v(-15, 108) * mm, "end": v(-33, 90) * mm});
            skLineSegment(sketch, "E84", {"start": v(15, 120) * mm, "end": v(15, 108) * mm});
            skLineSegment(sketch, "E85", {"start": v(15, 108) * mm, "end": v(33, 90) * mm});
            skLineSegment(sketch, "E86", {"start": v(-33, 90) * mm, "end": v(33, 90) * mm});
            skLineSegment(sketch, "E87", {"start": v(0, 90) * mm, "end": v(0, -89.48) * mm, "construction": true});
            skPoint(sketch, "E87.endSnap0", {"position": v(0, -90) * mm});
            skLineSegment(sketch, "E88", {"start": v(-89.5, 0) * mm, "end": v(95.8, 0) * mm, "construction": true});
            skPoint(sketch, "E88.startSnap0", {"position": v(-80, 0) * mm});
            skLineSegment(sketch, "E89.MirrorCS", {"start": v(-15, -120) * mm, "end": v(-15, -108) * mm});
            skLineSegment(sketch, "E90.MirrorCS", {"start": v(15, -120) * mm, "end": v(15, -108) * mm});
            skLineSegment(sketch, "E91.MirrorCS", {"start": v(0, -90) * mm, "end": v(0, -120) * mm, "construction": true});
            skCircle(sketch, "E92.MirrorC", {"center": v(0, -120) * mm, "radius": 6 * mm});
            skArc(sketch, "E93.MirrorCS", {"start": v(-15, -120) * mm, "mid": v(0, -135) * mm, "end": v(15, -120) * mm});
            skLineSegment(sketch, "E94.MirrorCS", {"start": v(-15, -108) * mm, "end": v(-33, -90) * mm});
            skLineSegment(sketch, "E95.MirrorCS", {"start": v(-33, -90) * mm, "end": v(33, -90) * mm});
            skLineSegment(sketch, "E96.MirrorCS", {"start": v(15, -108) * mm, "end": v(33, -90) * mm});
            skSolve(sketch);
        }
        {
            var Q0;
            {var subQ4=sQuery(id+"F16.wireOp",EDGE,"E86");Q0=makeQuery(id+"F16.imprint","IMPRINT",FACE,{"disambiguationData":[TD([[makeQuery(id+"F16.imprint","IMPRINT",EDGE,{"derivedFrom":subQ4}),-1.0]])]});}
            var Q1;
            Q1=makeQuery(id+"F16.imprint","IMPRINT",FACE,{"disambiguationData":[TD([[makeQuery(id+"F16.imprint","IMPRINT",EDGE,{"derivedFrom":sQuery(id+"F16.wireOp",EDGE,"E80")}),-1.0]])]});
            var Q2;
            Q2=makeQuery(id+"F16.imprint","IMPRINT",FACE,{"disambiguationData":[TD([[makeQuery(id+"F16.imprint","IMPRINT",EDGE,{"derivedFrom":sQuery(id+"F16.wireOp",EDGE,"E89.MirrorCS")}),-1.0]])]});
            var Q3;
            Q3=makeQuery(id+"F2.opExtrude","CAP_FACE",FACE,{"disambiguationData":[OSD([sQuery(id+"F0.wireOp",EDGE,"E12"),sQuery(id+"F0.wireOp",EDGE,"E13"),sQuery(id+"F0.wireOp",EDGE,"E14"),sQuery(id+"F0.wireOp",EDGE,"E15"),sQuery(id+"F0.wireOp",EDGE,"E17.filletArc"),sQuery(id+"F0.wireOp",EDGE,"E18.filletArc"),sQuery(id+"F0.wireOp",EDGE,"E19.filletArc"),sQuery(id+"F0.wireOp",EDGE,"E20.filletArc"),sQuery(id+"F0.wireOp",EDGE,"E25.0"),sQuery(id+"F0.wireOp",EDGE,"E25.1"),sQuery(id+"F0.wireOp",EDGE,"E25.2"),sQuery(id+"F0.wireOp",EDGE,"E25.3"),sQuery(id+"F0.wireOp",EDGE,"E25.4"),sQuery(id+"F0.wireOp",EDGE,"E25.5"),sQuery(id+"F0.wireOp",EDGE,"E25.6"),sQuery(id+"F0.wireOp",EDGE,"E25.7")])],"isStart":false});
            extrude(context, id + "F17", {"entities" : qUnion([Q0, Q1, Q2]), "endBound" : BoundingType.UP_TO_SURFACE, "depth" : 3 * mm, "endBoundEntityFace" : qUnion([Q3]), "offsetDistance" : 25 * mm});
        }
    });
